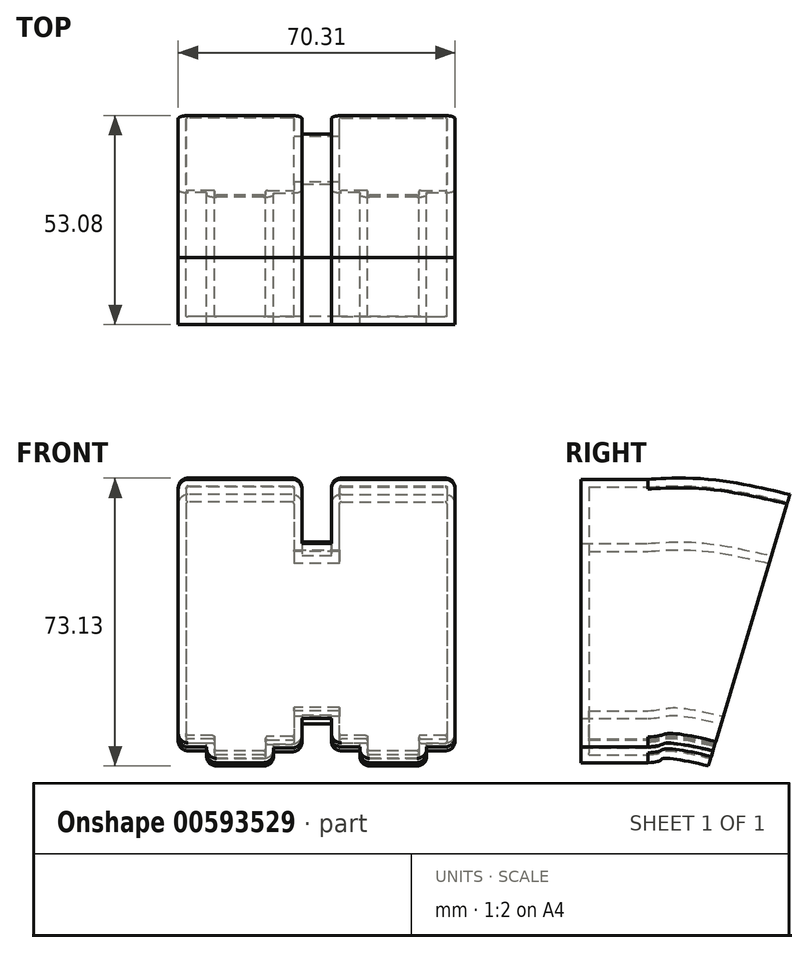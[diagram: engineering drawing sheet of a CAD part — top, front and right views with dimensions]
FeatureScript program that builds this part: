
annotation { "Feature Type Name" : "Feature", "Feature Type Description" : "" }
export const myFeature = defineFeature(function(context is Context, id is Id, definition is map)
    precondition{}
    {
        {
            var Q0;
            Q0=qCreatedBy(makeId("Front.planeOp"),FACE);
            var sketch = newSketch(context, id + "F0", { "sketchPlane" : qUnion([Q0])});
            skLineSegment(sketch, "E0.bottom", {"start": v(-98.87, 14.98) * mm, "end": v(-125.27, 14.98) * mm});
            skLineSegment(sketch, "E0.top", {"start": v(-106.07, -53.02) * mm, "end": v(-118.07, -53.02) * mm});
            skLineSegment(sketch, "E0.left", {"start": v(-98.37, 14.48) * mm, "end": v(-98.37, -48.8) * mm});
            skLineSegment(sketch, "E0.right", {"start": v(-125.77, 14.48) * mm, "end": v(-125.77, -48.52) * mm});
            skLineSegment(sketch, "E1.right", {"start": v(-86.86, -1.3) * mm, "end": v(-86.86, -41.84) * mm});
            skLineSegment(sketch, "E2", {"start": v(-86.86, -1.3) * mm, "end": v(-86.86, 14.48) * mm});
            skLineSegment(sketch, "E3", {"start": v(-86.36, 14.98) * mm, "end": v(-59.96, 14.98) * mm});
            skLineSegment(sketch, "E4", {"start": v(-59.46, 14.48) * mm, "end": v(-59.46, -48.52) * mm});
            skLineSegment(sketch, "E5", {"start": v(-67.16, -53.02) * mm, "end": v(-79.16, -53.02) * mm});
            skLineSegment(sketch, "E6", {"start": v(-86.86, -48.52) * mm, "end": v(-86.86, -41.84) * mm});
            skPoint(sketch, "E7.endSnap0", {"position": v(-112.07, -53.02) * mm});
            skLineSegment(sketch, "E8", {"start": v(-118.57, -49.52) * mm, "end": v(-118.57, -52.52) * mm});
            skLineSegment(sketch, "E9", {"start": v(-105.57, -49.8) * mm, "end": v(-105.57, -52.52) * mm});
            skLineSegment(sketch, "E10", {"start": v(-119.07, -49.02) * mm, "end": v(-125.27, -49.02) * mm});
            skLineSegment(sketch, "E11", {"start": v(-105.07, -49.3) * mm, "end": v(-98.87, -49.3) * mm});
            skPoint(sketch, "E12.orphan", {"position": v(-98.37, -53.02) * mm});
            skPoint(sketch, "E13.orphan", {"position": v(-125.77, -53.02) * mm});
            skPoint(sketch, "E7.end.orphan", {"position": v(-112.07, -49.02) * mm});
            skPoint(sketch, "E7.start.orphan", {"position": v(-112.07, -53.02) * mm});
            skPoint(sketch, "E14.visualSharp", {"position": v(-105.57, -53.02) * mm});
            skArc(sketch, "E14.filletArc", {"start": v(-106.07, -53.02) * mm, "mid": v(-105.71, -52.88) * mm, "end": v(-105.57, -52.52) * mm});
            skPoint(sketch, "E15.visualSharp", {"position": v(-118.57, -53.02) * mm});
            skArc(sketch, "E15.filletArc", {"start": v(-118.57, -52.52) * mm, "mid": v(-118.42, -52.88) * mm, "end": v(-118.07, -53.02) * mm});
            skPoint(sketch, "E16.visualSharp", {"position": v(-118.57, -49.02) * mm});
            skArc(sketch, "E16.filletArc", {"start": v(-118.57, -49.52) * mm, "mid": v(-118.71, -49.17) * mm, "end": v(-119.07, -49.02) * mm});
            skPoint(sketch, "E17.visualSharp", {"position": v(-105.57, -49.3) * mm});
            skArc(sketch, "E17.filletArc", {"start": v(-105.07, -49.3) * mm, "mid": v(-105.42, -49.44) * mm, "end": v(-105.57, -49.8) * mm});
            skPoint(sketch, "E18.visualSharp", {"position": v(-98.37, -49.3) * mm});
            skArc(sketch, "E18.filletArc", {"start": v(-98.87, -49.3) * mm, "mid": v(-98.51, -49.14) * mm, "end": v(-98.37, -48.8) * mm});
            skPoint(sketch, "E19.visualSharp", {"position": v(-125.77, -49.02) * mm});
            skArc(sketch, "E19.filletArc", {"start": v(-125.77, -48.52) * mm, "mid": v(-125.62, -48.88) * mm, "end": v(-125.27, -49.02) * mm});
            skPoint(sketch, "E20.visualSharp", {"position": v(-98.37, 14.98) * mm});
            skArc(sketch, "E20.filletArc", {"start": v(-98.37, 14.48) * mm, "mid": v(-98.51, 14.83) * mm, "end": v(-98.87, 14.98) * mm});
            skPoint(sketch, "E21.visualSharp", {"position": v(-125.77, 14.98) * mm});
            skArc(sketch, "E21.filletArc", {"start": v(-125.27, 14.98) * mm, "mid": v(-125.62, 14.83) * mm, "end": v(-125.77, 14.48) * mm});
            skPoint(sketch, "E22.visualSharp", {"position": v(-86.86, 14.98) * mm});
            skArc(sketch, "E22.filletArc", {"start": v(-86.36, 14.98) * mm, "mid": v(-86.71, 14.83) * mm, "end": v(-86.86, 14.48) * mm});
            skPoint(sketch, "E23.visualSharp", {"position": v(-59.46, 14.98) * mm});
            skArc(sketch, "E23.filletArc", {"start": v(-59.46, 14.48) * mm, "mid": v(-59.6, 14.83) * mm, "end": v(-59.96, 14.98) * mm});
            skLineSegment(sketch, "E24", {"start": v(-79.66, -49.52) * mm, "end": v(-79.66, -52.52) * mm});
            skLineSegment(sketch, "E25", {"start": v(-66.66, -49.52) * mm, "end": v(-66.66, -52.52) * mm});
            skLineSegment(sketch, "E26", {"start": v(-80.16, -49.02) * mm, "end": v(-86.36, -49.02) * mm});
            skLineSegment(sketch, "E27", {"start": v(-66.16, -49.02) * mm, "end": v(-59.96, -49.02) * mm});
            skPoint(sketch, "E28.start.orphan", {"position": v(-73.16, -53.02) * mm});
            skPoint(sketch, "E29.orphan", {"position": v(-86.86, -53.02) * mm});
            skPoint(sketch, "E30.orphan", {"position": v(-59.46, -53.02) * mm});
            skPoint(sketch, "E31.visualSharp", {"position": v(-79.66, -49.02) * mm});
            skArc(sketch, "E31.filletArc", {"start": v(-79.66, -49.52) * mm, "mid": v(-79.8, -49.17) * mm, "end": v(-80.16, -49.02) * mm});
            skPoint(sketch, "E32.visualSharp", {"position": v(-86.86, -49.02) * mm});
            skArc(sketch, "E32.filletArc", {"start": v(-86.86, -48.52) * mm, "mid": v(-86.71, -48.88) * mm, "end": v(-86.36, -49.02) * mm});
            skPoint(sketch, "E33.visualSharp", {"position": v(-79.66, -53.02) * mm});
            skArc(sketch, "E33.filletArc", {"start": v(-79.66, -52.52) * mm, "mid": v(-79.51, -52.88) * mm, "end": v(-79.16, -53.02) * mm});
            skPoint(sketch, "E34.visualSharp", {"position": v(-66.66, -53.02) * mm});
            skArc(sketch, "E34.filletArc", {"start": v(-67.16, -53.02) * mm, "mid": v(-66.8, -52.88) * mm, "end": v(-66.66, -52.52) * mm});
            skPoint(sketch, "E35.visualSharp", {"position": v(-66.66, -49.02) * mm});
            skArc(sketch, "E35.filletArc", {"start": v(-66.16, -49.02) * mm, "mid": v(-66.51, -49.17) * mm, "end": v(-66.66, -49.52) * mm});
            skPoint(sketch, "E36.visualSharp", {"position": v(-59.46, -49.02) * mm});
            skArc(sketch, "E36.filletArc", {"start": v(-59.96, -49.02) * mm, "mid": v(-59.6, -48.88) * mm, "end": v(-59.46, -48.52) * mm});
            skLineSegment(sketch, "E37", {"start": v(-86.86, -41.84) * mm, "end": v(-98.37, -41.84) * mm});
            skLineSegment(sketch, "E38", {"start": v(-86.86, -1.3) * mm, "end": v(-98.37, -1.3) * mm});
            skSolve(sketch);
        }
        {
            var Q0;
            Q0=qSketchRegion(id+"F0",true);
            extrude(context, id + "F1", {"entities" : qUnion([Q0]), "depth" : 15 * mm, "offsetDistance" : 25 * mm});
        }
        {
            var Q0;
            Q0=makeQuery(id+"F1.opExtrude","CAP_FACE",FACE,{"disambiguationData":[OSD([sQuery(id+"F0.wireOp",EDGE,"E0.bottom"),sQuery(id+"F0.wireOp",EDGE,"E0.top"),sQuery(id+"F0.wireOp",EDGE,"E0.left"),sQuery(id+"F0.wireOp",EDGE,"E0.right"),sQuery(id+"F0.wireOp",EDGE,"E2"),sQuery(id+"F0.wireOp",EDGE,"E3"),sQuery(id+"F0.wireOp",EDGE,"E4"),sQuery(id+"F0.wireOp",EDGE,"E5"),sQuery(id+"F0.wireOp",EDGE,"E6"),sQuery(id+"F0.wireOp",EDGE,"E8"),sQuery(id+"F0.wireOp",EDGE,"E9"),sQuery(id+"F0.wireOp",EDGE,"E10"),sQuery(id+"F0.wireOp",EDGE,"E11"),sQuery(id+"F0.wireOp",EDGE,"E14.filletArc"),sQuery(id+"F0.wireOp",EDGE,"E15.filletArc"),sQuery(id+"F0.wireOp",EDGE,"E16.filletArc"),sQuery(id+"F0.wireOp",EDGE,"E17.filletArc"),sQuery(id+"F0.wireOp",EDGE,"E18.filletArc"),sQuery(id+"F0.wireOp",EDGE,"E19.filletArc"),sQuery(id+"F0.wireOp",EDGE,"E20.filletArc"),sQuery(id+"F0.wireOp",EDGE,"E21.filletArc"),sQuery(id+"F0.wireOp",EDGE,"E22.filletArc"),sQuery(id+"F0.wireOp",EDGE,"E23.filletArc"),sQuery(id+"F0.wireOp",EDGE,"E24"),sQuery(id+"F0.wireOp",EDGE,"E25"),sQuery(id+"F0.wireOp",EDGE,"E26"),sQuery(id+"F0.wireOp",EDGE,"E27"),sQuery(id+"F0.wireOp",EDGE,"E31.filletArc"),sQuery(id+"F0.wireOp",EDGE,"E32.filletArc"),sQuery(id+"F0.wireOp",EDGE,"E33.filletArc"),sQuery(id+"F0.wireOp",EDGE,"E34.filletArc"),sQuery(id+"F0.wireOp",EDGE,"E35.filletArc"),sQuery(id+"F0.wireOp",EDGE,"E36.filletArc"),sQuery(id+"F0.wireOp",EDGE,"CR1f763u-fsqj-ihyr-gCo7-DafutXi8A8ZV"),sQuery(id+"F0.wireOp",EDGE,"ysZW6Lni-AIO4-wqFM-19ql-4kTzM9Co0uhU")])],"isStart":true});
            shell(context, id + "F2", {"entities" : qUnion([Q0]), "thickness" : 2 * mm, "oppositeDirection" : true});
        }
        {
            var Q0;
            Q0=qCreatedBy(makeId("Right.planeOp"),FACE);
            var sketch = newSketch(context, id + "F3", { "sketchPlane" : qUnion([Q0])});
            skLineSegment(sketch, "E39", {"start": v(0, 17.17) * mm, "end": v(0, -56.83) * mm});
            skLineSegment(sketch, "E40", {"start": v(0, -56.83) * mm, "end": v(0, -19.83) * mm});
            skLineSegment(sketch, "E41", {"start": v(0, -19.83) * mm, "end": v(3.14, -19.83) * mm});
            skPoint(sketch, "E42.1.internal.snap0", {"position": v(3.14, -19.83) * mm});
            skPoint(sketch, "E43.orphan", {"position": v(6.27, -19.83) * mm});
            skFitSpline(sketch, "E44", {"points": [v(3.14, -19.83) * mm, v(12.17, -19.83) * mm, v(28.49, -23.04) * mm], "startDerivative": vector(19.79, 1.18) * mm, "endDerivative": vector(30.38, -7.18) * mm});
            skSolve(sketch);
        }
        {
            var Q0;
            Q0=makeQuery(id+"F1.opExtrude","CAP_FACE",FACE,{"disambiguationData":[OSD([sQuery(id+"F0.wireOp",EDGE,"E0.bottom"),sQuery(id+"F0.wireOp",EDGE,"E0.top"),sQuery(id+"F0.wireOp",EDGE,"E0.left"),sQuery(id+"F0.wireOp",EDGE,"E0.right"),sQuery(id+"F0.wireOp",EDGE,"E2"),sQuery(id+"F0.wireOp",EDGE,"E3"),sQuery(id+"F0.wireOp",EDGE,"E4"),sQuery(id+"F0.wireOp",EDGE,"E5"),sQuery(id+"F0.wireOp",EDGE,"E6"),sQuery(id+"F0.wireOp",EDGE,"E8"),sQuery(id+"F0.wireOp",EDGE,"E9"),sQuery(id+"F0.wireOp",EDGE,"E10"),sQuery(id+"F0.wireOp",EDGE,"E11"),sQuery(id+"F0.wireOp",EDGE,"E14.filletArc"),sQuery(id+"F0.wireOp",EDGE,"E15.filletArc"),sQuery(id+"F0.wireOp",EDGE,"E16.filletArc"),sQuery(id+"F0.wireOp",EDGE,"E17.filletArc"),sQuery(id+"F0.wireOp",EDGE,"E18.filletArc"),sQuery(id+"F0.wireOp",EDGE,"E19.filletArc"),sQuery(id+"F0.wireOp",EDGE,"E20.filletArc"),sQuery(id+"F0.wireOp",EDGE,"E21.filletArc"),sQuery(id+"F0.wireOp",EDGE,"E22.filletArc"),sQuery(id+"F0.wireOp",EDGE,"E23.filletArc"),sQuery(id+"F0.wireOp",EDGE,"E24"),sQuery(id+"F0.wireOp",EDGE,"E25"),sQuery(id+"F0.wireOp",EDGE,"E26"),sQuery(id+"F0.wireOp",EDGE,"E27"),sQuery(id+"F0.wireOp",EDGE,"E31.filletArc"),sQuery(id+"F0.wireOp",EDGE,"E32.filletArc"),sQuery(id+"F0.wireOp",EDGE,"E33.filletArc"),sQuery(id+"F0.wireOp",EDGE,"E34.filletArc"),sQuery(id+"F0.wireOp",EDGE,"E35.filletArc"),sQuery(id+"F0.wireOp",EDGE,"E36.filletArc"),sQuery(id+"F0.wireOp",EDGE,"E37"),sQuery(id+"F0.wireOp",EDGE,"E38")])],"isStart":true});
            var Q1;
            Q1=sQuery(id+"F3.wireOp",EDGE,"E44");
            sweep(context, id + "F4", {"operationType" : NewBodyOperationType.ADD, "profiles" : qUnion([Q0]), "path" : qUnion([Q1])});
        }
    });
